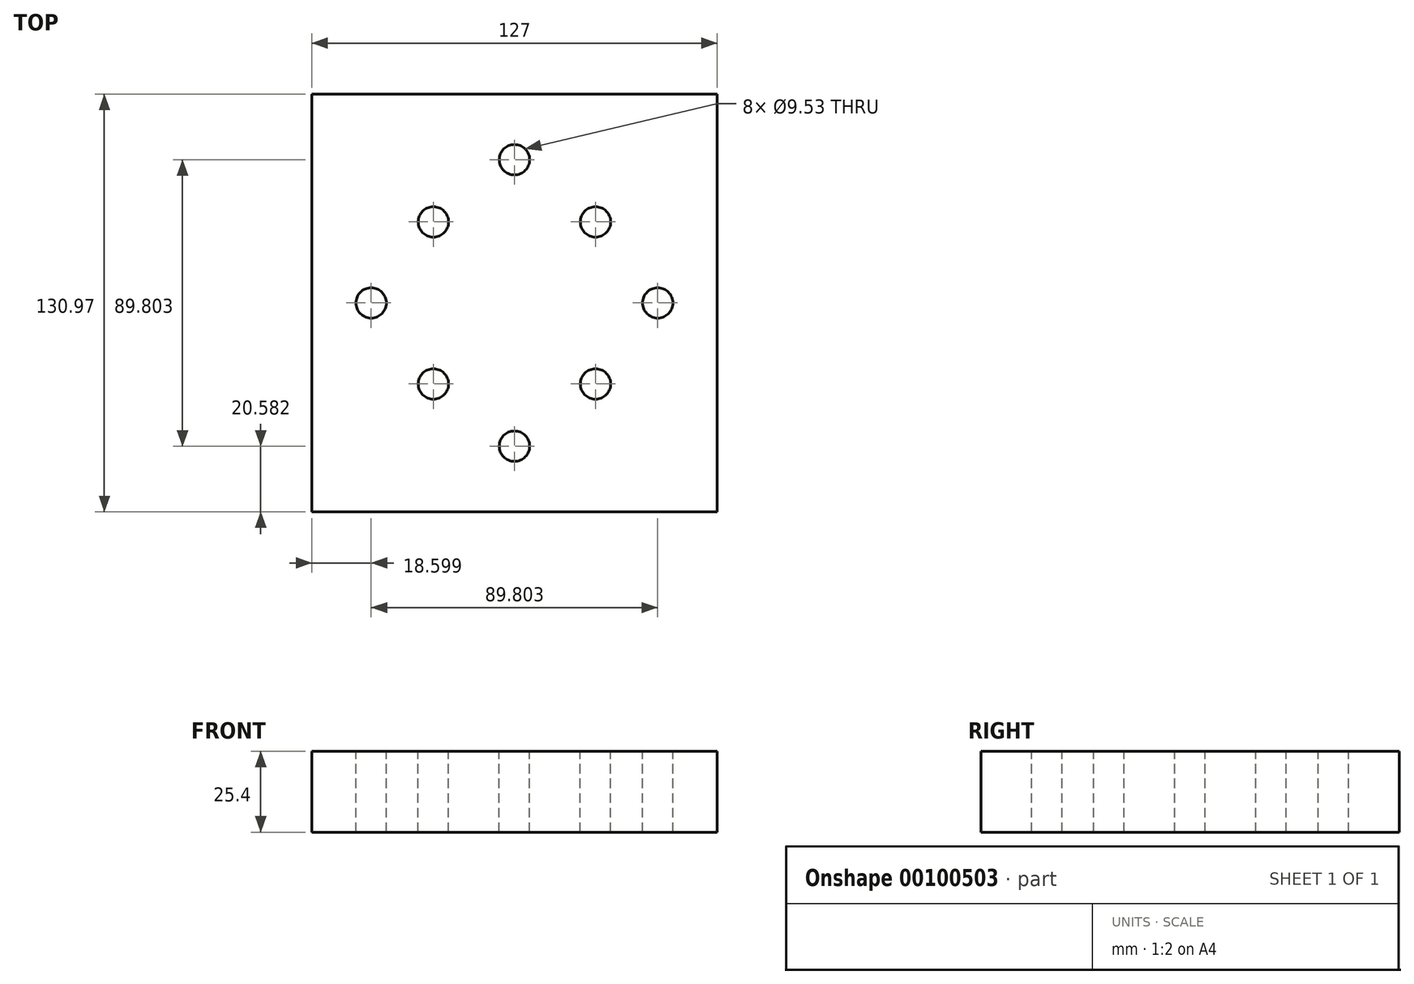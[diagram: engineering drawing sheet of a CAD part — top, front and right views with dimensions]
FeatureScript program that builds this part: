
annotation { "Feature Type Name" : "Feature", "Feature Type Description" : "" }
export const myFeature = defineFeature(function(context is Context, id is Id, definition is map)
    precondition{}
    {
        {
            var Q0;
            Q0=qCreatedBy(makeId("Top.planeOp"),FACE);
            var sketch = newSketch(context, id + "F0", { "sketchPlane" : qUnion([Q0])});
            skLineSegment(sketch, "E0.bottom", {"start": v(0, 0) * mm, "end": v(127, 0) * mm});
            skLineSegment(sketch, "E0.top", {"start": v(0, 130.97) * mm, "end": v(127, 130.97) * mm});
            skLineSegment(sketch, "E0.left", {"start": v(0, 0) * mm, "end": v(0, 130.97) * mm});
            skLineSegment(sketch, "E0.right", {"start": v(127, 0) * mm, "end": v(127, 130.97) * mm});
            skCircle(sketch, "E1", {"center": v(63.5, 110.39) * mm, "radius": 4.76 * mm});
            skCircle(sketch, "E2", {"center": v(108.4, 65.48) * mm, "radius": 4.76 * mm});
            skCircle(sketch, "E3", {"center": v(18.6, 65.48) * mm, "radius": 4.76 * mm});
            skCircle(sketch, "E4", {"center": v(63.5, 20.58) * mm, "radius": 4.76 * mm});
            skCircle(sketch, "E5", {"center": v(88.9, 90.88) * mm, "radius": 4.76 * mm});
            skCircle(sketch, "E6", {"center": v(88.9, 40.08) * mm, "radius": 4.76 * mm});
            skCircle(sketch, "E7", {"center": v(38.1, 40.08) * mm, "radius": 4.76 * mm});
            skCircle(sketch, "E8", {"center": v(38.1, 90.88) * mm, "radius": 4.76 * mm});
            skSolve(sketch);
        }
        {
            var Q0;
            Q0 = qSketchRegion(id + "F0", true);
            extrude(context, id + "F1", {"entities" : qUnion([Q0]), "oppositeDirection" : true, "depth" : 25.4 * mm});
        }
    });
